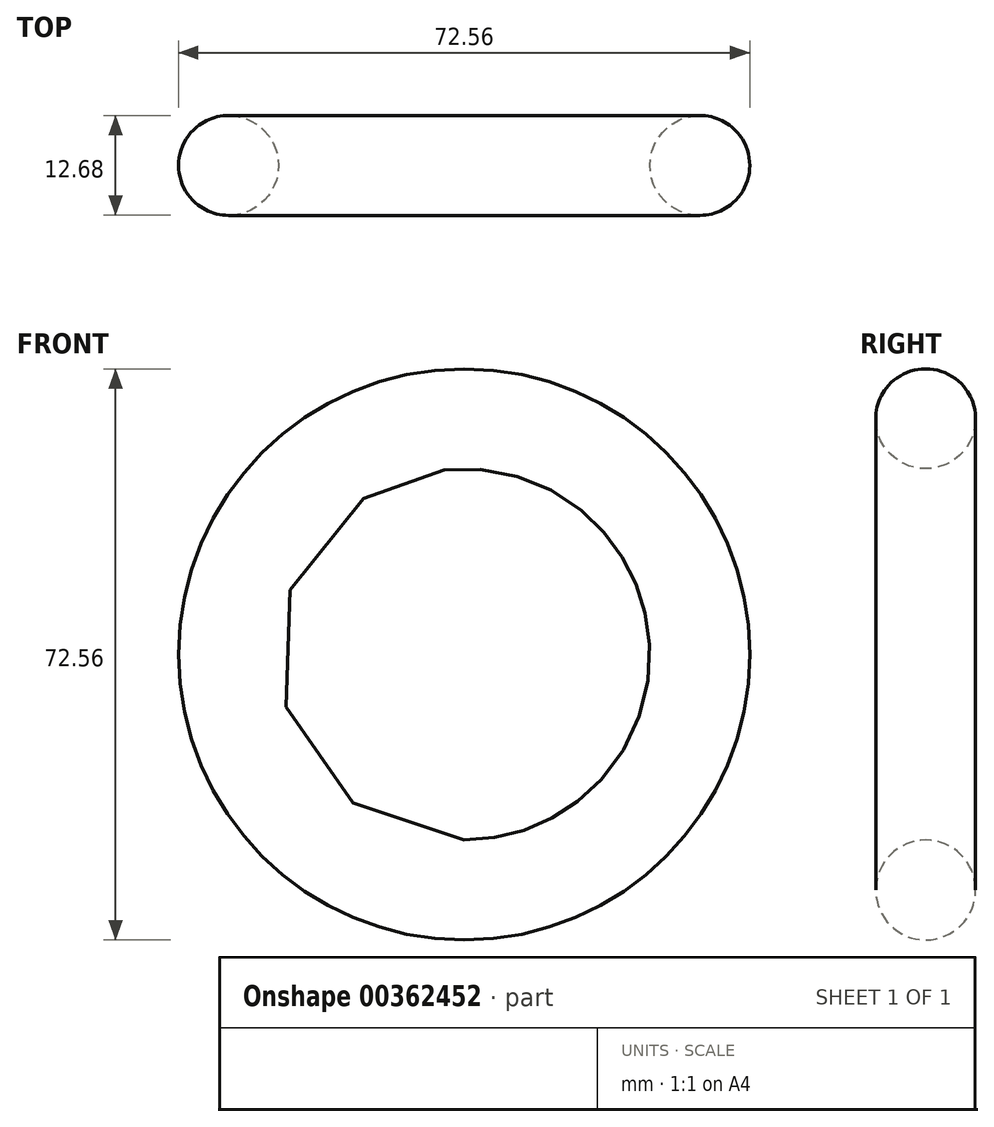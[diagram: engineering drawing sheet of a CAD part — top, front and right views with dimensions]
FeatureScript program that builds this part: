
annotation { "Feature Type Name" : "Feature", "Feature Type Description" : "" }
export const myFeature = defineFeature(function(context is Context, id is Id, definition is map)
    precondition{}
    {
        {
            var Q0;
            Q0=qCreatedBy(makeId("Front.planeOp"),FACE);
            var sketch = newSketch(context, id + "F0", { "sketchPlane" : qUnion([Q0])});
            skCircle(sketch, "E0", {"center": v(0, 0) * mm, "radius": 30.06 * mm});
            skSolve(sketch);
        }
        {
            var Q0;
            Q0=qCreatedBy(makeId("Top.planeOp"),FACE);
            var sketch = newSketch(context, id + "F1", { "sketchPlane" : qUnion([Q0])});
            skCircle(sketch, "E1", {"center": v(-29.93, 0) * mm, "radius": 6.34 * mm});
            skSolve(sketch);
        }
        {
            var Q0;
            Q0=makeQuery(id+"F1.imprint","IMPRINT",FACE,{"disambiguationData":[TD([[makeQuery(id+"F1.imprint","IMPRINT",EDGE,{"derivedFrom":sQuery(id+"F1.wireOp",EDGE,"E1")}),1.0]])]});
            var Q1;
            Q1=sQuery(id+"F0.wireOp",EDGE,"E0");
            sweep(context, id + "F2", {"profiles" : qUnion([Q0]), "path" : qUnion([Q1])});
        }
    });
